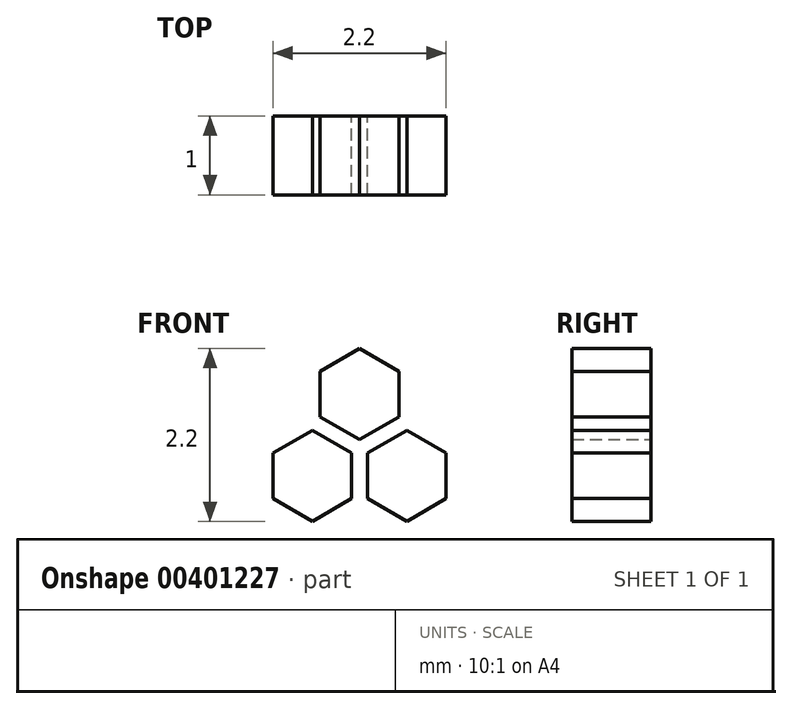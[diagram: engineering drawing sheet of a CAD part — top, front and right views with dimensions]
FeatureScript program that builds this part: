
annotation { "Feature Type Name" : "Feature", "Feature Type Description" : "" }
export const myFeature = defineFeature(function(context is Context, id is Id, definition is map)
    precondition{}
    {
        {
            var Q0;
            Q0=qCreatedBy(makeId("Front.planeOp"),FACE);
            var sketch = newSketch(context, id + "F0", { "sketchPlane" : qUnion([Q0])});
            skCircle(sketch, "E0.cCircle", {"center": v(0, 0) * mm, "radius": 0.5 * mm, "construction": true});
            skLineSegment(sketch, "E0.0", {"start": v(0.5, 0.29) * mm, "end": v(0.5, -0.29) * mm});
            skLineSegment(sketch, "E0.1", {"start": v(0.5, -0.29) * mm, "end": v(0, -0.58) * mm});
            skLineSegment(sketch, "E0.2", {"start": v(0, -0.58) * mm, "end": v(-0.5, -0.29) * mm});
            skLineSegment(sketch, "E0.3", {"start": v(-0.5, -0.29) * mm, "end": v(-0.5, 0.29) * mm});
            skLineSegment(sketch, "E0.4", {"start": v(-0.5, 0.29) * mm, "end": v(0, 0.58) * mm});
            skLineSegment(sketch, "E0.5", {"start": v(0, 0.58) * mm, "end": v(0.5, 0.29) * mm});
            skPoint(sketch, "E0.0.midPoint", {"position": v(0.5, 0) * mm});
            skLineSegment(sketch, "E1", {"start": v(0, 0) * mm, "end": v(1.3, 0) * mm, "construction": true});
            skCircle(sketch, "E2.cCircle", {"center": v(1.2, 0) * mm, "radius": 0.5 * mm, "construction": true});
            skLineSegment(sketch, "E2.0", {"start": v(1.7, 0.29) * mm, "end": v(1.7, -0.29) * mm});
            skLineSegment(sketch, "E2.1", {"start": v(1.7, -0.29) * mm, "end": v(1.2, -0.58) * mm});
            skLineSegment(sketch, "E2.2", {"start": v(1.2, -0.58) * mm, "end": v(0.7, -0.29) * mm});
            skLineSegment(sketch, "E2.3", {"start": v(0.7, -0.29) * mm, "end": v(0.7, 0.29) * mm});
            skLineSegment(sketch, "E2.4", {"start": v(0.7, 0.29) * mm, "end": v(1.2, 0.58) * mm});
            skLineSegment(sketch, "E2.5", {"start": v(1.2, 0.58) * mm, "end": v(1.7, 0.29) * mm});
            skPoint(sketch, "E2.0.midPoint", {"position": v(1.7, 0) * mm});
            skCircle(sketch, "E3.cCircle", {"center": v(0.6, 1.04) * mm, "radius": 0.5 * mm, "construction": true});
            skLineSegment(sketch, "E3.0", {"start": v(1.1, 1.33) * mm, "end": v(1.1, 0.75) * mm});
            skLineSegment(sketch, "E3.1", {"start": v(1.1, 0.75) * mm, "end": v(0.6, 0.46) * mm});
            skLineSegment(sketch, "E3.2", {"start": v(0.6, 0.46) * mm, "end": v(0.1, 0.75) * mm});
            skLineSegment(sketch, "E3.3", {"start": v(0.1, 0.75) * mm, "end": v(0.1, 1.33) * mm});
            skLineSegment(sketch, "E3.4", {"start": v(0.1, 1.33) * mm, "end": v(0.6, 1.62) * mm});
            skLineSegment(sketch, "E3.5", {"start": v(0.6, 1.62) * mm, "end": v(1.1, 1.33) * mm});
            skPoint(sketch, "E3.0.midPoint", {"position": v(1.1, 1.04) * mm});
            skSolve(sketch);
        }
        {
            var Q0;
            Q0=makeQuery(id+"F0.imprint","IMPRINT",FACE,{"disambiguationData":[TD([[makeQuery(id+"F0.imprint","IMPRINT",EDGE,{"derivedFrom":sQuery(id+"F0.wireOp",EDGE,"E0.0")}),-1.0]])]});
            var Q1;
            Q1=makeQuery(id+"F0.imprint","IMPRINT",FACE,{"disambiguationData":[TD([[makeQuery(id+"F0.imprint","IMPRINT",EDGE,{"derivedFrom":sQuery(id+"F0.wireOp",EDGE,"E3.0")}),-1.0]])]});
            var Q2;
            Q2=makeQuery(id+"F0.imprint","IMPRINT",FACE,{"disambiguationData":[TD([[makeQuery(id+"F0.imprint","IMPRINT",EDGE,{"derivedFrom":sQuery(id+"F0.wireOp",EDGE,"E2.0")}),-1.0]])]});
            extrude(context, id + "F1", {"entities" : qUnion([Q0, Q1, Q2]), "depth" : 1 * mm});
        }
    });
